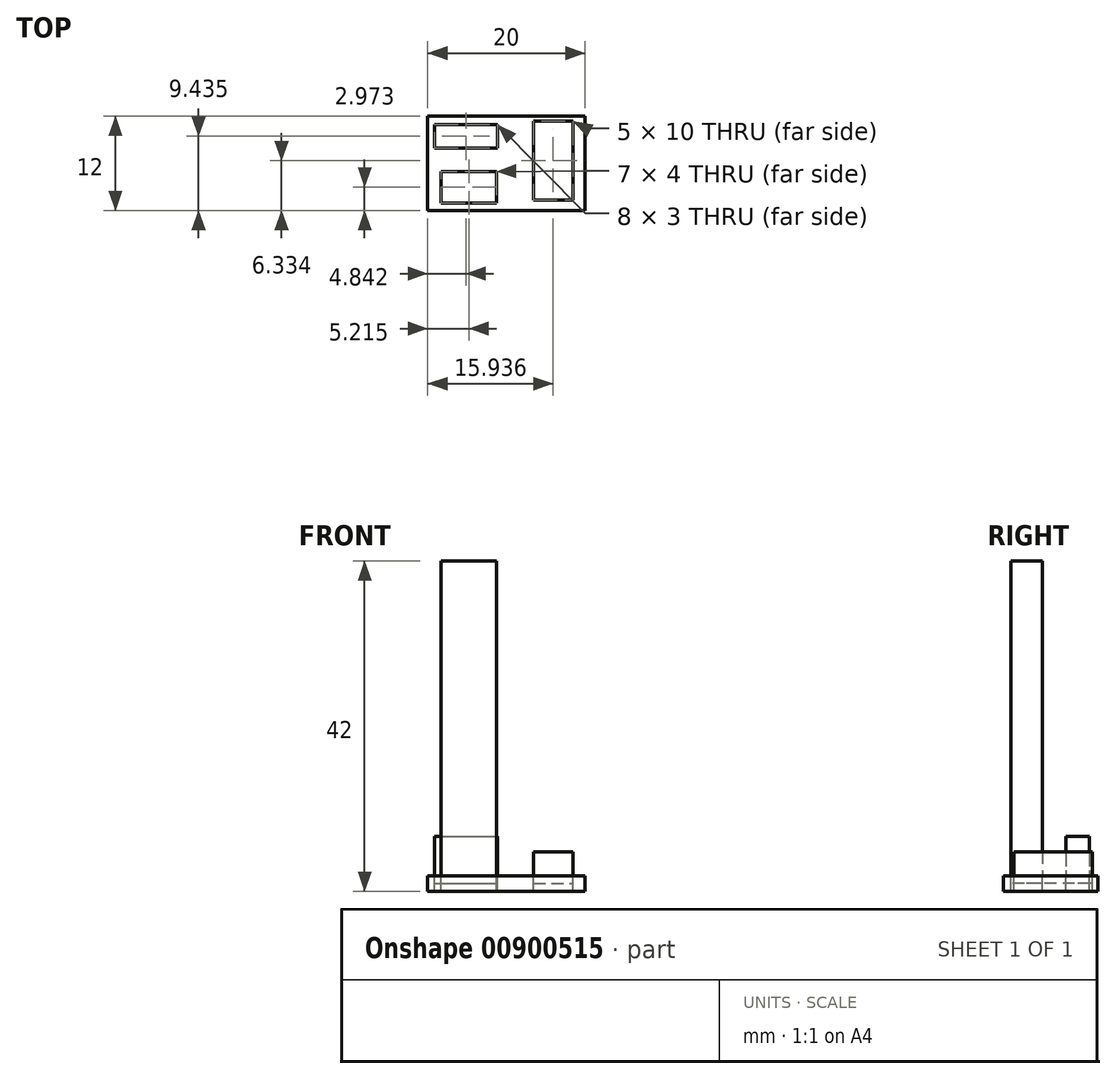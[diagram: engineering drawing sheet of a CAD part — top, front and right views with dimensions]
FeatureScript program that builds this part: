
annotation { "Feature Type Name" : "Feature", "Feature Type Description" : "" }
export const myFeature = defineFeature(function(context is Context, id is Id, definition is map)
    precondition{}
    {
        {
            var Q0;
            Q0=qCreatedBy(makeId("Top.planeOp"),FACE);
            var sketch = newSketch(context, id + "F0", { "sketchPlane" : qUnion([Q0])});
            skLineSegment(sketch, "E0.bottom", {"start": v(0, 0) * mm, "end": v(-20, 0) * mm});
            skLineSegment(sketch, "E0.top", {"start": v(0, 12) * mm, "end": v(-20, 12) * mm});
            skLineSegment(sketch, "E0.left", {"start": v(0, 0) * mm, "end": v(0, 12) * mm});
            skLineSegment(sketch, "E0.right", {"start": v(-20, 0) * mm, "end": v(-20, 12) * mm});
            skLineSegment(sketch, "E1.bottom", {"start": v(-20, 6) * mm, "end": v(0, 6) * mm, "construction": true});
            skLineSegment(sketch, "E1.top", {"start": v(-20, 6) * mm, "end": v(0, 6) * mm, "construction": true});
            skLineSegment(sketch, "E1.left", {"start": v(-20, 6) * mm, "end": v(-20, 6) * mm});
            skLineSegment(sketch, "E1.right", {"start": v(0, 6) * mm, "end": v(0, 6) * mm});
            skLineSegment(sketch, "E2", {"start": v(-10, 12) * mm, "end": v(-10, 0) * mm, "construction": true});
            skLineSegment(sketch, "E3.bottom", {"start": v(-18.29, 4.97) * mm, "end": v(-11.29, 4.97) * mm, "construction": true});
            skLineSegment(sketch, "E3.top", {"start": v(-18.29, 0.97) * mm, "end": v(-11.29, 0.97) * mm, "construction": true});
            skLineSegment(sketch, "E3.left", {"start": v(-18.29, 4.97) * mm, "end": v(-18.29, 0.97) * mm, "construction": true});
            skLineSegment(sketch, "E3.right", {"start": v(-11.29, 4.97) * mm, "end": v(-11.29, 0.97) * mm, "construction": true});
            skLineSegment(sketch, "E4.bottom", {"start": v(-19.16, 10.94) * mm, "end": v(-11.16, 10.94) * mm});
            skLineSegment(sketch, "E4.top", {"start": v(-19.16, 7.94) * mm, "end": v(-11.16, 7.94) * mm});
            skLineSegment(sketch, "E4.left", {"start": v(-19.16, 10.94) * mm, "end": v(-19.16, 7.94) * mm});
            skLineSegment(sketch, "E4.right", {"start": v(-11.16, 10.94) * mm, "end": v(-11.16, 7.94) * mm});
            skLineSegment(sketch, "E5.bottom", {"start": v(-18.29, 4.97) * mm, "end": v(-11.29, 4.97) * mm});
            skLineSegment(sketch, "E5.top", {"start": v(-18.29, 0.97) * mm, "end": v(-11.29, 0.97) * mm});
            skLineSegment(sketch, "E5.left", {"start": v(-18.29, 4.97) * mm, "end": v(-18.29, 0.97) * mm});
            skLineSegment(sketch, "E5.right", {"start": v(-11.29, 4.97) * mm, "end": v(-11.29, 0.97) * mm});
            skLineSegment(sketch, "E6.bottom", {"start": v(-6.56, 11.33) * mm, "end": v(-1.56, 11.33) * mm});
            skLineSegment(sketch, "E6.top", {"start": v(-6.56, 1.33) * mm, "end": v(-1.56, 1.33) * mm});
            skLineSegment(sketch, "E6.left", {"start": v(-6.56, 11.33) * mm, "end": v(-6.56, 1.33) * mm});
            skLineSegment(sketch, "E6.right", {"start": v(-1.56, 11.33) * mm, "end": v(-1.56, 1.33) * mm});
            skSolve(sketch);
        }
        {
            var Q0;
            Q0=makeQuery(id+"F0.imprint","IMPRINT",FACE,{"disambiguationData":[TD([[makeQuery(id+"F0.imprint","IMPRINT",EDGE,{"derivedFrom":sQuery(id+"F0.wireOp",EDGE,"E4.bottom")}),-1.0]])]});
            extrude(context, id + "F1", {"entities" : qUnion([Q0]), "depth" : 5 * mm, "offsetDistance" : 25 * mm});
        }
        {
            var Q0;
            Q0=makeQuery(id+"F0.imprint","IMPRINT",FACE,{"disambiguationData":[TD([[makeQuery(id+"F0.imprint","IMPRINT",EDGE,{"derivedFrom":sQuery(id+"F0.wireOp",EDGE,"E5.bottom")}),-1.0]])]});
            extrude(context, id + "F2", {"entities" : qUnion([Q0]), "depth" : 40 * mm, "offsetDistance" : 25 * mm});
        }
        {
            var Q0;
            Q0=makeQuery(id+"F0.imprint","IMPRINT",FACE,{"disambiguationData":[TD([[makeQuery(id+"F0.imprint","IMPRINT",EDGE,{"derivedFrom":sQuery(id+"F0.wireOp",EDGE,"E6.bottom")}),-1.0]])]});
            extrude(context, id + "F3", {"entities" : qUnion([Q0]), "depth" : 3 * mm, "offsetDistance" : 25 * mm});
        }
        {
            var Q0;
            Q0=makeQuery(id+"F0.imprint","IMPRINT",FACE,{"disambiguationData":[TD([[makeQuery(id+"F0.imprint","IMPRINT",EDGE,{"derivedFrom":sQuery(id+"F0.wireOp",EDGE,"E0.bottom")}),-1.0]])]});
            extrude(context, id + "F4", {"entities" : qUnion([Q0]), "oppositeDirection" : true, "depth" : 2 * mm, "offsetDistance" : 25 * mm});
        }
        {
            var Q0;
            Q0=makeQuery(id+"F0.imprint","IMPRINT",FACE,{"disambiguationData":[TD([[makeQuery(id+"F0.imprint","IMPRINT",EDGE,{"derivedFrom":sQuery(id+"F0.wireOp",EDGE,"E5.bottom")}),-1.0]])]});
            var Q1;
            Q1=makeQuery(id+"F0.imprint","IMPRINT",FACE,{"disambiguationData":[TD([[makeQuery(id+"F0.imprint","IMPRINT",EDGE,{"derivedFrom":sQuery(id+"F0.wireOp",EDGE,"E4.bottom")}),-1.0]])]});
            var Q2;
            Q2=makeQuery(id+"F0.imprint","IMPRINT",FACE,{"disambiguationData":[TD([[makeQuery(id+"F0.imprint","IMPRINT",EDGE,{"derivedFrom":sQuery(id+"F0.wireOp",EDGE,"E6.bottom")}),-1.0]])]});
            extrude(context, id + "F5", {"entities" : qUnion([Q0, Q1, Q2]), "oppositeDirection" : true, "depth" : 1 * mm, "offsetDistance" : 25 * mm});
        }
    });
